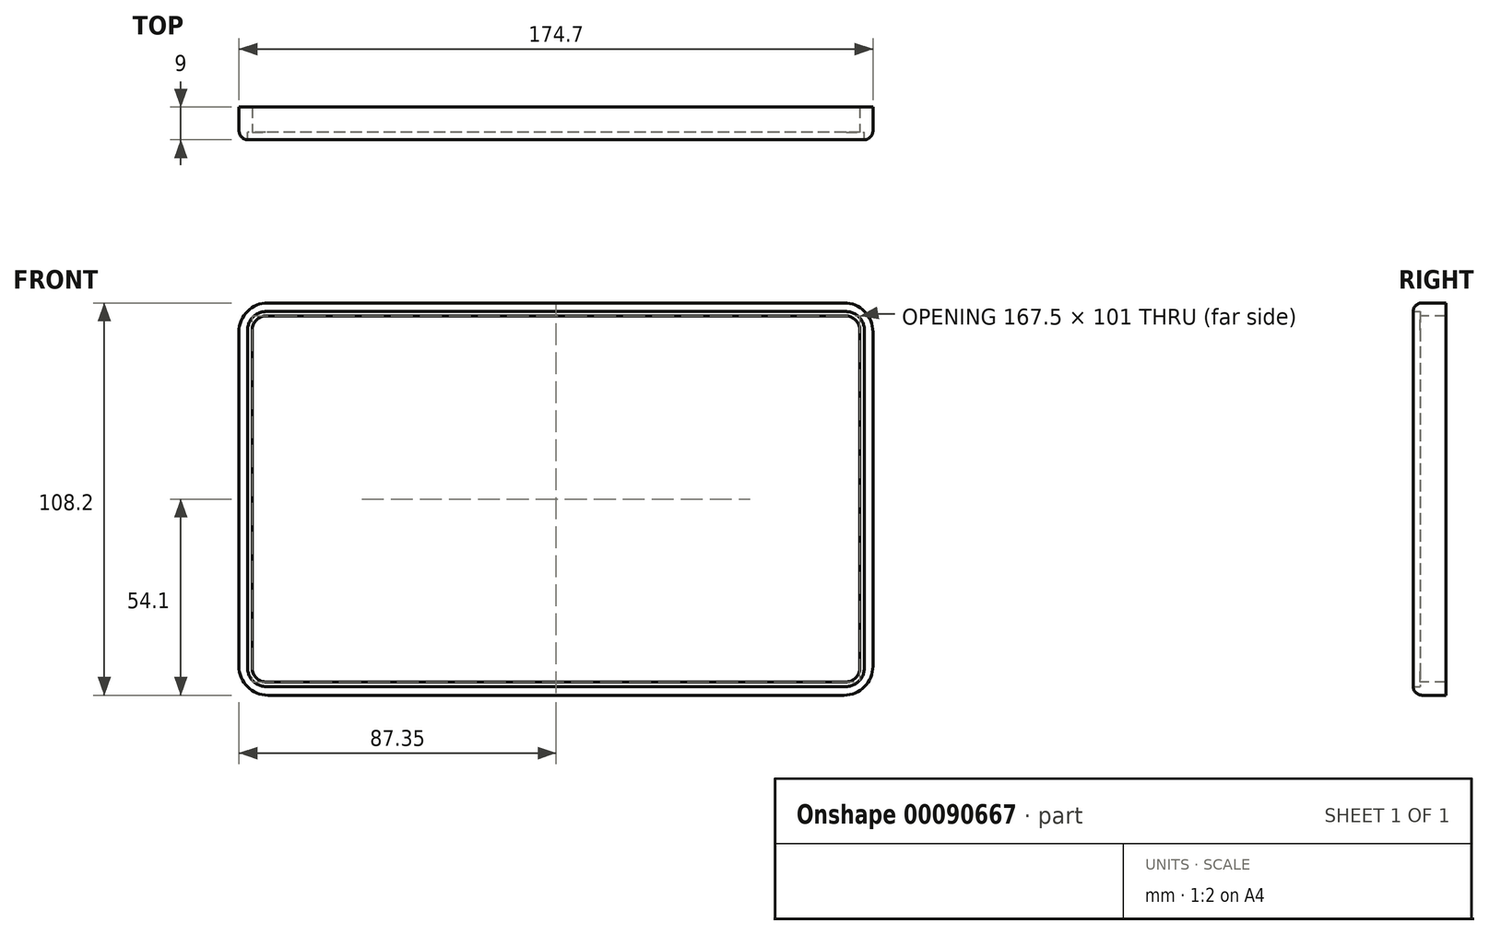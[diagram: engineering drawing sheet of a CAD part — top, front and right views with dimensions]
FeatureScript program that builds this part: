
annotation { "Feature Type Name" : "Feature", "Feature Type Description" : "" }
export const myFeature = defineFeature(function(context is Context, id is Id, definition is map)
    precondition{}
    {
        {
            var Q0;
            Q0=qCreatedBy(makeId("Front.planeOp"),FACE);
            var sketch = newSketch(context, id + "F0", { "sketchPlane" : qUnion([Q0])});
            skLineSegment(sketch, "E0.bottom", {"start": v(83.75, 50.5) * mm, "end": v(-83.75, 50.5) * mm});
            skLineSegment(sketch, "E0.top", {"start": v(83.75, -50.5) * mm, "end": v(-83.75, -50.5) * mm});
            skLineSegment(sketch, "E0.left", {"start": v(83.75, 50.5) * mm, "end": v(83.75, -50.5) * mm});
            skLineSegment(sketch, "E0.right", {"start": v(-83.75, 50.5) * mm, "end": v(-83.75, -50.5) * mm});
            skPoint(sketch, "E0.middle", {"position": v(0, 0) * mm});
            skLineSegment(sketch, "E1.0", {"start": v(84.95, 51.7) * mm, "end": v(-84.95, 51.7) * mm});
            skLineSegment(sketch, "E1.1", {"start": v(84.95, 51.7) * mm, "end": v(84.95, -51.7) * mm});
            skLineSegment(sketch, "E1.2", {"start": v(84.95, -51.7) * mm, "end": v(-84.95, -51.7) * mm});
            skLineSegment(sketch, "E1.3", {"start": v(-84.95, 51.7) * mm, "end": v(-84.95, -51.7) * mm});
            skLineSegment(sketch, "E2.0", {"start": v(87.35, 54.1) * mm, "end": v(87.35, -54.1) * mm});
            skLineSegment(sketch, "E2.1", {"start": v(87.35, 54.1) * mm, "end": v(-87.35, 54.1) * mm});
            skLineSegment(sketch, "E2.2", {"start": v(-87.35, 54.1) * mm, "end": v(-87.35, -54.1) * mm});
            skLineSegment(sketch, "E2.3", {"start": v(87.35, -54.1) * mm, "end": v(-87.35, -54.1) * mm});
            skSolve(sketch);
        }
        {
            var Q0;
            Q0=makeQuery(id+"F0.imprint","IMPRINT",FACE,{"disambiguationData":[TD([[makeQuery(id+"F0.imprint","IMPRINT",EDGE,{"derivedFrom":sQuery(id+"F0.wireOp",EDGE,"E1.0")}),-1.0]])]});
            extrude(context, id + "F1", {"entities" : qUnion([Q0]), "depth" : 2 * mm});
        }
        {
            var Q0;
            Q0=makeQuery(id+"F0.imprint","IMPRINT",FACE,{"disambiguationData":[TD([[makeQuery(id+"F0.imprint","IMPRINT",EDGE,{"derivedFrom":sQuery(id+"F0.wireOp",EDGE,"E0.bottom")}),-1.0]])]});
            var Q1;
            Q1=makeQuery(id+"F0.imprint","IMPRINT",FACE,{"disambiguationData":[TD([[makeQuery(id+"F0.imprint","IMPRINT",EDGE,{"derivedFrom":sQuery(id+"F0.wireOp",EDGE,"E1.0")}),-1.0]])]});
            extrude(context, id + "F2", {"entities" : qUnion([Q0, Q1]), "operationType" : NewBodyOperationType.ADD, "oppositeDirection" : true, "depth" : 7 * mm});
        }
        {
            var Q0;
            Q0=makeQuery(id+"F2.opExtrude","SWEPT_EDGE",EDGE,{"disambiguationData":[OSD([sQuery(id+"F0.wireOp",EDGE,"E0.bottom"),sQuery(id+"F0.wireOp",EDGE,"E0.left")])]});
            var Q1;
            Q1=makeQuery(id+"F2.opExtrude","SWEPT_EDGE",EDGE,{"disambiguationData":[OSD([sQuery(id+"F0.wireOp",EDGE,"E0.bottom"),sQuery(id+"F0.wireOp",EDGE,"E0.right")])]});
            var Q2;
            Q2=makeQuery(id+"F2.opExtrude","SWEPT_EDGE",EDGE,{"disambiguationData":[OSD([sQuery(id+"F0.wireOp",EDGE,"E0.top"),sQuery(id+"F0.wireOp",EDGE,"E0.right")])]});
            var Q3;
            Q3=makeQuery(id+"F2.opExtrude","SWEPT_EDGE",EDGE,{"disambiguationData":[OSD([sQuery(id+"F0.wireOp",EDGE,"E0.top"),sQuery(id+"F0.wireOp",EDGE,"E0.left")])]});
            fillet(context, id + "F3", {"entities" : qUnion([Q0, Q1, Q2, Q3]), "radius" : 4 * mm, "tangentPropagation" : true, "allowEdgeOverflow" : false});
        }
        {
            var Q0;
            Q0=makeQuery(id+"F1.opExtrude","SWEPT_EDGE",EDGE,{"disambiguationData":[OSD([sQuery(id+"F0.wireOp",EDGE,"E1.0"),sQuery(id+"F0.wireOp",EDGE,"E1.1")])]});
            var Q1;
            Q1=makeQuery(id+"F1.opExtrude","SWEPT_EDGE",EDGE,{"disambiguationData":[OSD([sQuery(id+"F0.wireOp",EDGE,"E1.1"),sQuery(id+"F0.wireOp",EDGE,"E1.2")])]});
            var Q2;
            Q2=makeQuery(id+"F1.opExtrude","SWEPT_EDGE",EDGE,{"disambiguationData":[OSD([sQuery(id+"F0.wireOp",EDGE,"E1.2"),sQuery(id+"F0.wireOp",EDGE,"E1.3")])]});
            var Q3;
            Q3=makeQuery(id+"F1.opExtrude","SWEPT_EDGE",EDGE,{"disambiguationData":[OSD([sQuery(id+"F0.wireOp",EDGE,"E1.0"),sQuery(id+"F0.wireOp",EDGE,"E1.3")])]});
            fillet(context, id + "F4", {"entities" : qUnion([Q0, Q1, Q2, Q3]), "radius" : 5 * mm, "tangentPropagation" : true, "allowEdgeOverflow" : false});
        }
        {
            var Q0;
            {var subQ0=sQuery(id+"F0.wireOp",EDGE,"E2.3");var subQ1=sQuery(id+"F0.wireOp",EDGE,"E2.0");Q0=makeQuery(id+"F2.boolean.opBoolean","MERGE",EDGE,{"derivedFrom":[makeQuery(id+"F1.opExtrude","SWEPT_EDGE",EDGE,{"disambiguationData":[OSD([subQ1,subQ0])]}),makeQuery(id+"F2.opExtrude","SWEPT_EDGE",EDGE,{"disambiguationData":[OSD([subQ1,subQ0])]})]});}
            var Q1;
            {var subQ0=sQuery(id+"F0.wireOp",EDGE,"E2.3");var subQ1=sQuery(id+"F0.wireOp",EDGE,"E2.2");Q1=makeQuery(id+"F2.boolean.opBoolean","MERGE",EDGE,{"derivedFrom":[makeQuery(id+"F1.opExtrude","SWEPT_EDGE",EDGE,{"disambiguationData":[OSD([subQ1,subQ0])]}),makeQuery(id+"F2.opExtrude","SWEPT_EDGE",EDGE,{"disambiguationData":[OSD([subQ1,subQ0])]})]});}
            var Q2;
            {var subQ0=sQuery(id+"F0.wireOp",EDGE,"E2.2");var subQ1=sQuery(id+"F0.wireOp",EDGE,"E2.1");Q2=makeQuery(id+"F2.boolean.opBoolean","MERGE",EDGE,{"derivedFrom":[makeQuery(id+"F1.opExtrude","SWEPT_EDGE",EDGE,{"disambiguationData":[OSD([subQ1,subQ0])]}),makeQuery(id+"F2.opExtrude","SWEPT_EDGE",EDGE,{"disambiguationData":[OSD([subQ1,subQ0])]})]});}
            var Q3;
            {var subQ0=sQuery(id+"F0.wireOp",EDGE,"E2.1");var subQ1=sQuery(id+"F0.wireOp",EDGE,"E2.0");Q3=makeQuery(id+"F2.boolean.opBoolean","MERGE",EDGE,{"derivedFrom":[makeQuery(id+"F1.opExtrude","SWEPT_EDGE",EDGE,{"disambiguationData":[OSD([subQ1,subQ0])]}),makeQuery(id+"F2.opExtrude","SWEPT_EDGE",EDGE,{"disambiguationData":[OSD([subQ1,subQ0])]})]});}
            fillet(context, id + "F5", {"entities" : qUnion([Q0, Q1, Q2, Q3]), "radius" : 8 * mm, "tangentPropagation" : true, "allowEdgeOverflow" : false});
        }
        {
            var Q0;
            {var subQ0=sQuery(id+"F0.wireOp",EDGE,"E2.2");var subQ1=sQuery(id+"F0.wireOp",EDGE,"E2.1");Q0=makeQuery(id+"F5.opFillet","BLEND_EDGE",EDGE,{"blendedFrom":[makeQuery(id+"F2.boolean.opBoolean","MERGE",EDGE,{"derivedFrom":[makeQuery(id+"F1.opExtrude","SWEPT_EDGE",EDGE,{"disambiguationData":[OSD([subQ1,subQ0])]}),makeQuery(id+"F2.opExtrude","SWEPT_EDGE",EDGE,{"disambiguationData":[OSD([subQ1,subQ0])]})]}),makeQuery(id+"F1.opExtrude","CAP_FACE",FACE,{"disambiguationData":[OSD([sQuery(id+"F0.wireOp",EDGE,"E1.0"),sQuery(id+"F0.wireOp",EDGE,"E1.1"),sQuery(id+"F0.wireOp",EDGE,"E1.2"),sQuery(id+"F0.wireOp",EDGE,"E1.3"),sQuery(id+"F0.wireOp",EDGE,"E2.0"),subQ1,subQ0,sQuery(id+"F0.wireOp",EDGE,"E2.3")])],"isStart":false})],"blendedInto":[makeQuery(id+"F1.opExtrude","CAP_FACE",FACE,{"disambiguationData":[OSD([sQuery(id+"F0.wireOp",EDGE,"E1.0"),sQuery(id+"F0.wireOp",EDGE,"E1.1"),sQuery(id+"F0.wireOp",EDGE,"E1.2"),sQuery(id+"F0.wireOp",EDGE,"E1.3"),sQuery(id+"F0.wireOp",EDGE,"E2.0"),subQ1,subQ0,sQuery(id+"F0.wireOp",EDGE,"E2.3")])],"isStart":false})]});}
            fillet(context, id + "F6", {"entities" : qUnion([Q0]), "radius" : 2.5 * mm, "tangentPropagation" : true, "allowEdgeOverflow" : false});
        }
    });
